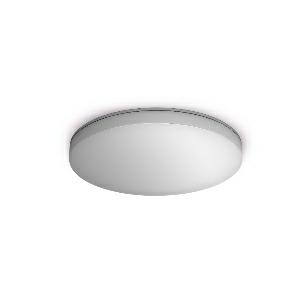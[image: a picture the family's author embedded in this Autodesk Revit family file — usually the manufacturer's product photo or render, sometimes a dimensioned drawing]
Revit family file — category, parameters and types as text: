
# Revit family: rs_pro_connect_r10_057039
name_source: partatom
category: Leuchten
revit_build: Autodesk Revit 2016 (Build: 20190508_0715(x64)
units: mm (PartAtom-declared; Revit-internal decimal feet)

## family parameters
Basisbauteil = Fläche
Beim Laden mit Abzugskörper schneiden = Nein
Bemaßung runder Anschluss = Durchmesser verwenden
Gemeinsam genutzt = Nein
Lichtquelle = Nein
Raumberechnungspunkt = Nein
Teiletyp = Normal

## types (1)
- RS PRO Connect R10 (1 x , 1100 lm, 3000 K)
    Beschreibung = Dimensions (Ø x H): 300 x 55 mm; Mains power supply: 220 – 240 V / 50 – 60 Hz; Sensor Technology: High frequency; Transmitter power: < 1 mW; HF-system: 5,8 GHz; Output: 9 W; Interconnection: Yes; Type of interconnection: Master/slave; Luminous flux: 1100 lm; Colour temperature: 3000 K; Colour variation LED: SDCM3; Colour Rendering Index CRI: 80-89; With lamp: Yes, STEINEL LED system; Lamp: LED cannot be replaced; LED life expectancy (max. °C): 55000 h; LED life expectancy (25 °C): 60000 h; Drop in luminous flux in accordance with LM80: L80B50; Base: without; LED cooling system: Passive Thermo Control; With motion detector: Yes; Detection: also through glass, wood and stud walls; Detection angle: 360 °; Angle of aperture: 160 °; Capability of masking out individual segments: Yes; Electronic scalability: Yes; Mechanical scalability: No; Reach, radial: Ø 10 m (79 m²); Reach, tangential: Ø 10 m (79 m²); Main light adjustable: 50 - 100 %; Continuous light: selectable; Photo-cell controller: Yes; Twilight setting: 2 – 2000 lx; Time setting: 5 sec – 30 min; Basic light level function: Yes; Basic light level function, detail: LED Backlight; Basic light level function time: 10-30 min, all night; Functions: Group parameterisation, Manual ON / ON-OFF, Master/slave override, Neighbouring-group function, Presence function, Backlight; Soft light start: Yes; Impact resistance: IK07; IP-rating: IP40; Protection class: II; Ambient temperature: -20 – 40 °C; Housing material: Plastic; Cover material: PC, opal; Manufacturer's Warranty: 5 years; Settings via: Bluetooth; With remote control: No; Version: warm white; PU1, EAN: 4007841057039
    CIE Flux Codes = 44 75 93 94 100
    Color Rendering = 80-89
    Color Temperature = 3000 K
    Frequency = 60 Hz, 50 Hz
    Height = 0 mm  [stored 0 ft]
    Hersteller = Steinel
    Lamp Light Flux = 1100 lm
    Lamp count = 1
    Lampe = 1 x
    Length = 300 mm
    Luminous efficacy = 0 lm/W
    ModVariant = Nein
    Modell = 057039
    Mounting Type = Surface mounted
    Number of Poles = 1
    OnlyDefault = Ja
    Power Factor = 1
    Product Name = RS PRO Connect R10
    Product group = Sensor-switched indoor light
    ProductGroupID = 30
    Protection Class = Protection class II
    Protection Degree = IP 40
    RlxData = <blob elided: 168245 chars, md5=cfe1d10b>
    Scheinlast = 0 VA
    Socket = socket
    Standby Power = 0 W
    System Light Flux = 0 lm
    System Power = 0 W
    Typenbild = produkt1_057039.jpg
    Typenkommentare = Product without accessories
    URL = http://relux.com
    VarID = ---
    Voltage = 0 V
    Vorgabe-Ansicht = 1800 mm
    Weight = 0.00 kg
    Width = 0 mm  [stored 0 ft]

note: [stored X ft] marks values corroborated as IEEE doubles in the binary element streams (Revit-internal decimal feet)

## geometry (parser evidence)
native form markers: Sweep x15
no freeform markers — native parametric forms only
